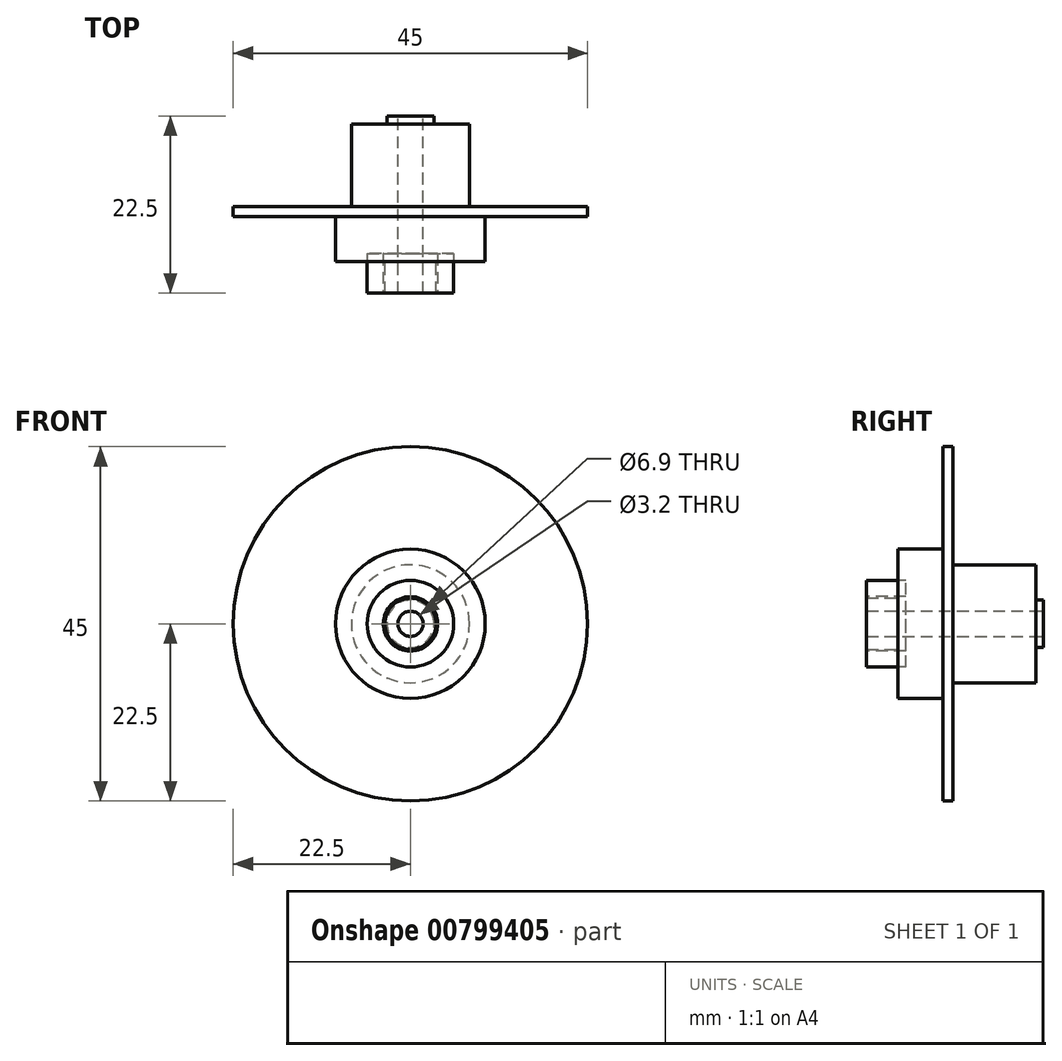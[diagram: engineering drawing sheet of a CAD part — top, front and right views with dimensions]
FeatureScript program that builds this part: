
annotation { "Feature Type Name" : "Feature", "Feature Type Description" : "" }
export const myFeature = defineFeature(function(context is Context, id is Id, definition is map)
    precondition{}
    {
        {
            var Q0;
            Q0=qCreatedBy(makeId("Front.planeOp"),FACE);
            var sketch = newSketch(context, id + "F0", { "sketchPlane" : qUnion([Q0])});
            skCircle(sketch, "E0", {"center": v(0, 0) * mm, "radius": 22.5 * mm});
            skCircle(sketch, "E1", {"center": v(0, 0) * mm, "radius": 1.6 * mm});
            skCircle(sketch, "E2", {"center": v(0, 0) * mm, "radius": 9.5 * mm});
            skSolve(sketch);
        }
        {
            var Q0;
            Q0 = qSketchRegion(id + "F0", true);
            var Q1;
            Q1=makeQuery(id+"F0.imprint","IMPRINT",FACE,{"disambiguationData":[TD([[makeQuery(id+"F0.imprint","IMPRINT",EDGE,{"derivedFrom":sQuery(id+"F0.wireOp",EDGE,"E0")}),1.0]])]});
            var Q2;
            Q2=makeQuery(id+"F0.imprint","IMPRINT",FACE,{"disambiguationData":[TD([[makeQuery(id+"F0.imprint","IMPRINT",EDGE,{"derivedFrom":sQuery(id+"F0.wireOp",EDGE,"E1")}),-1.0]])]});
            extrude(context, id + "F1", {"entities" : qUnion([Q0, Q1, Q2]), "depth" : 1.3 * mm, "offsetDistance" : 25 * mm});
        }
        {
            var Q0;
            Q0=makeQuery(id+"F0.imprint","IMPRINT",FACE,{"disambiguationData":[TD([[makeQuery(id+"F0.imprint","IMPRINT",EDGE,{"derivedFrom":sQuery(id+"F0.wireOp",EDGE,"E1")}),-1.0]])]});
            extrude(context, id + "F2", {"entities" : qUnion([Q0]), "operationType" : NewBodyOperationType.ADD, "depth" : 7 * mm, "offsetDistance" : 25 * mm});
        }
        {
            var Q0;
            Q0=makeQuery(id+"F2.opExtrude","CAP_FACE",FACE,{"disambiguationData":[OSD([sQuery(id+"F0.wireOp",EDGE,"E1"),sQuery(id+"F0.wireOp",EDGE,"E2")])],"isStart":false});
            var sketch = newSketch(context, id + "F3", { "sketchPlane" : qUnion([Q0])});
            skCircle(sketch, "E3", {"center": v(0, 0) * mm, "radius": 3.25 * mm});
            skSolve(sketch);
        }
        {
            var Q0;
            Q0=makeQuery(id+"F3.imprint","IMPRINT",FACE,{"disambiguationData":[TD([[makeQuery(id+"F3.imprint","IMPRINT",EDGE,{"derivedFrom":sQuery(id+"F3.wireOp",EDGE,"E3")}),1.0]])]});
            extrude(context, id + "F4", {"entities" : qUnion([Q0]), "operationType" : NewBodyOperationType.ADD, "depth" : 4 * mm, "offsetDistance" : 25 * mm});
        }
        {
            var Q0;
            Q0=makeQuery(id+"F1.opExtrude","CAP_FACE",FACE,{"disambiguationData":[OSD([sQuery(id+"F0.wireOp",EDGE,"E0"),sQuery(id+"F0.wireOp",EDGE,"E1")])],"isStart":true});
            var sketch = newSketch(context, id + "F5", { "sketchPlane" : qUnion([Q0])});
            skCircle(sketch, "E4", {"center": v(0, 0) * mm, "radius": 7.5 * mm});
            skSolve(sketch);
        }
        {
            var Q0;
            Q0=makeQuery(id+"F5.imprint","IMPRINT",FACE,{"disambiguationData":[TD([[makeQuery(id+"F5.imprint","IMPRINT",EDGE,{"derivedFrom":sQuery(id+"F5.wireOp",EDGE,"E4")}),1.0]])]});
            extrude(context, id + "F6", {"entities" : qUnion([Q0]), "operationType" : NewBodyOperationType.ADD, "depth" : 10.5 * mm, "offsetDistance" : 25 * mm});
        }
        {
            var Q0;
            Q0=makeQuery(id+"F6.opExtrude","CAP_FACE",FACE,{"disambiguationData":[OSD([sQuery(id+"F5.wireOp",EDGE,"E4")])],"isStart":false});
            var sketch = newSketch(context, id + "F7", { "sketchPlane" : qUnion([Q0])});
            skCircle(sketch, "E5", {"center": v(0, 0) * mm, "radius": 3 * mm});
            skSolve(sketch);
        }
        {
            var Q0;
            Q0=makeQuery(id+"F7.imprint","IMPRINT",FACE,{"disambiguationData":[TD([[makeQuery(id+"F7.imprint","IMPRINT",EDGE,{"derivedFrom":sQuery(id+"F7.wireOp",EDGE,"E5")}),1.0]])]});
            extrude(context, id + "F8", {"entities" : qUnion([Q0]), "operationType" : NewBodyOperationType.ADD, "depth" : 1 * mm, "offsetDistance" : 25 * mm});
        }
        {
            var Q0;
            Q0=makeQuery(id+"F4.opExtrude","CAP_FACE",FACE,{"disambiguationData":[OSD([sQuery(id+"F0.wireOp",EDGE,"E1"),sQuery(id+"F3.wireOp",EDGE,"E3")])],"isStart":false});
            var sketch = newSketch(context, id + "F9", { "sketchPlane" : qUnion([Q0])});
            skCircle(sketch, "E6", {"center": v(0, 0) * mm, "radius": 3.45 * mm});
            skCircle(sketch, "E7", {"center": v(0, 0) * mm, "radius": 5.5 * mm});
            skSolve(sketch);
        }
        {
            var Q0;
            Q0=makeQuery(id+"F9.imprint","IMPRINT",FACE,{"disambiguationData":[TD([[makeQuery(id+"F9.imprint","IMPRINT",EDGE,{"derivedFrom":sQuery(id+"F9.wireOp",EDGE,"E6")}),-1.0]])]});
            var Q1;
            Q1=makeQuery(id+"F2.opExtrude","CAP_FACE",FACE,{"disambiguationData":[OSD([sQuery(id+"F0.wireOp",EDGE,"E1"),sQuery(id+"F0.wireOp",EDGE,"E2")])],"isStart":false});
            extrude(context, id + "F10", {"entities" : qUnion([Q0]), "oppositeDirection" : true, "depth" : 5 * mm, "endBoundEntityFace" : qUnion([Q1]), "offsetDistance" : 0.1 * mm});
        }
    });
